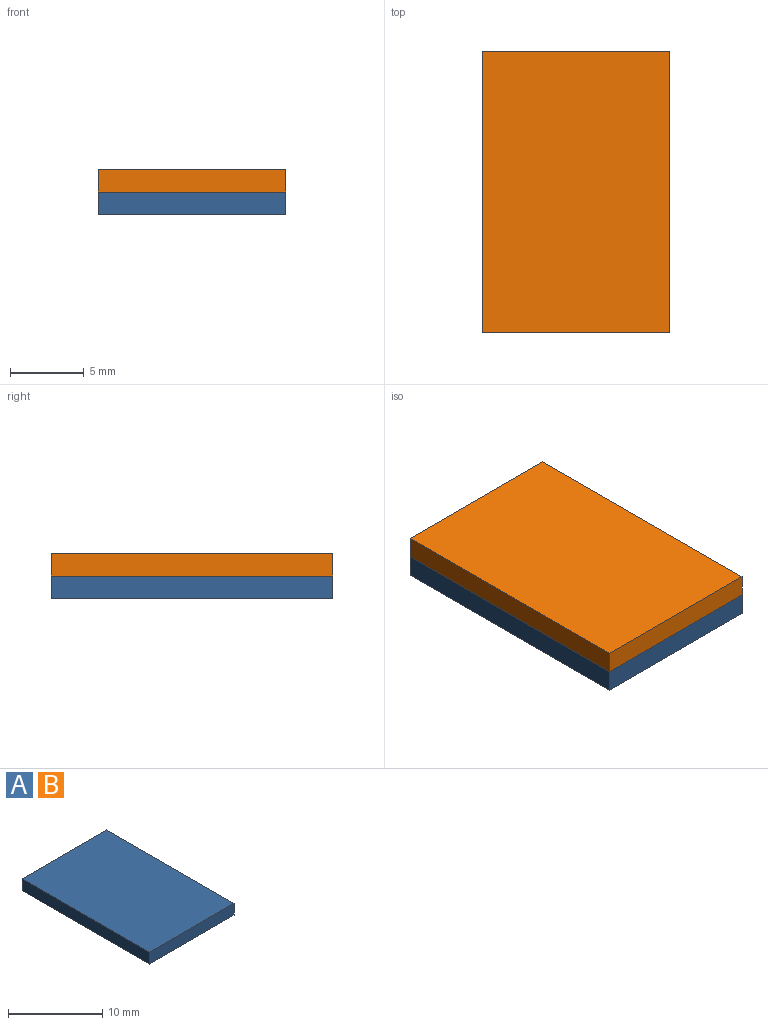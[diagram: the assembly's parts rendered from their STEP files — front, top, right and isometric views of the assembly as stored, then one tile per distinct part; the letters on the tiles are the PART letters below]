
ASSEMBLY  parts=2 mates=1
PART A: 6 faces, bbox 12.7x19.1x1.5 mm
  f0: plane 12.7x1.52mm, normal (0,-1,0), area 19.4mm2, adj f1,f3,f4,f5
  f1: plane 19.05x1.52mm, normal (1,0,0), area 29mm2, adj f0,f2,f4,f5
  f2: plane 12.7x1.52mm, normal (0,1,0), area 19.4mm2, adj f1,f3,f4,f5
  f3: plane 19.05x1.52mm, normal (-1,0,0), area 29mm2, adj f0,f2,f4,f5
  f4: plane 19.05x12.7mm, normal (0,0,1), area 241.9mm2, adj f0,f1,f2,f3
  f5: plane 19.05x12.7mm, normal (0,0,-1), area 241.9mm2, adj f0,f1,f2,f3
PART B: same geometry as A
PLACE A t=(-259.56,7.18,-29.55)mm
PLACE B t=(-259.56,7.18,-28.02)mm
MATE fastened B.f5 <-> A.f4  axis (0,0,-1) through (-259.56,7.18,-28.02)mm
